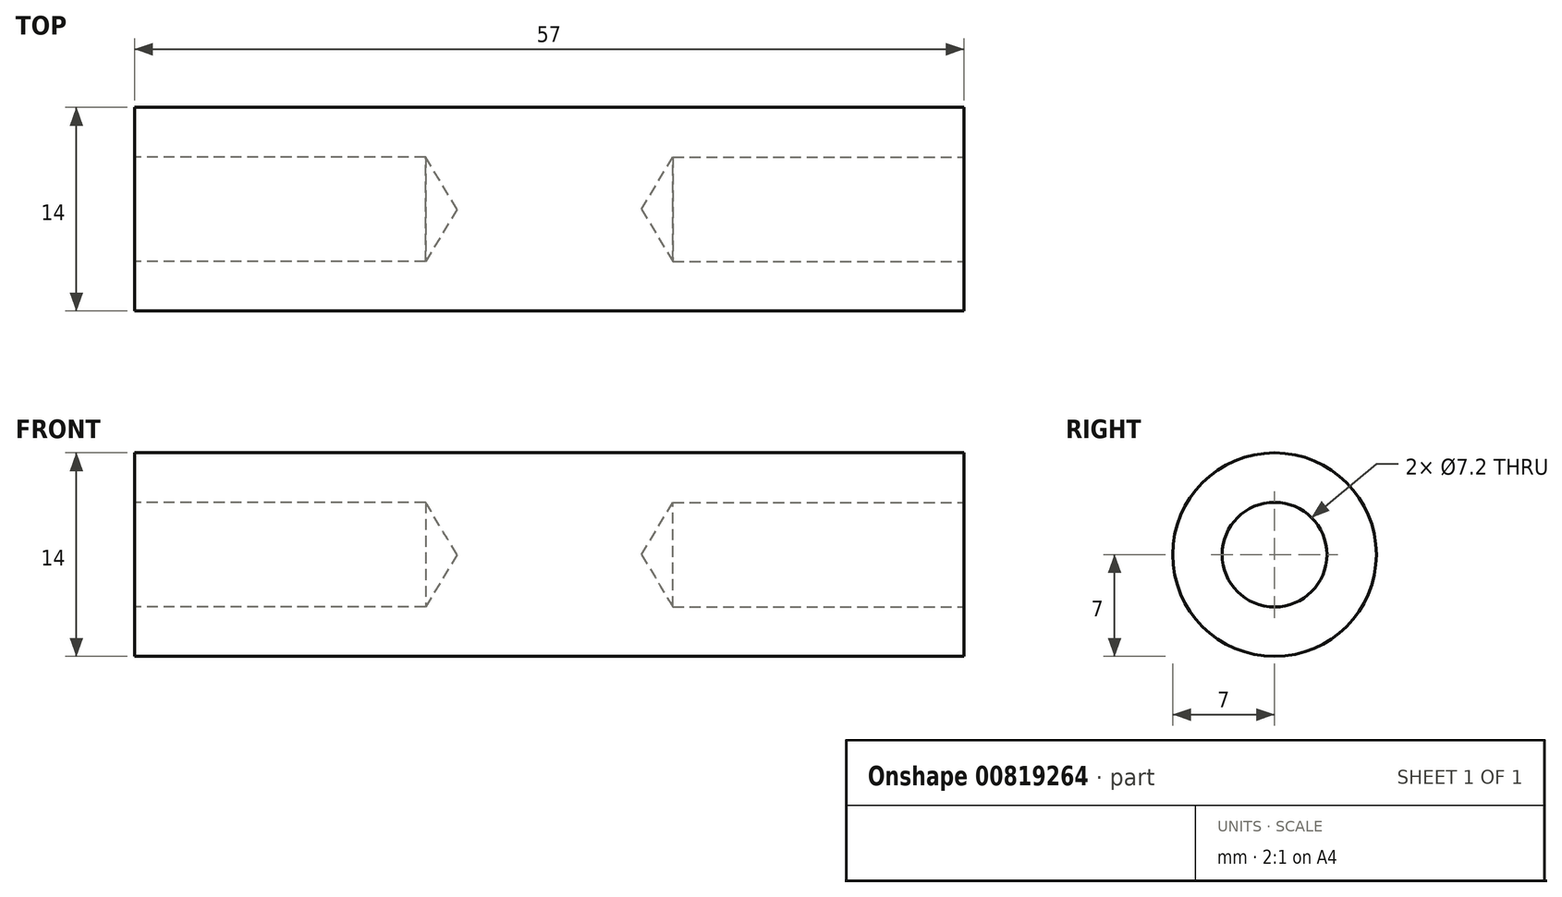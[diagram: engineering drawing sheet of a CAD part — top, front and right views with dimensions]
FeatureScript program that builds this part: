
annotation { "Feature Type Name" : "Feature", "Feature Type Description" : "" }
export const myFeature = defineFeature(function(context is Context, id is Id, definition is map)
    precondition{}
    {
        {
            var Q0;
            Q0=qCreatedBy(makeId("Front.planeOp"),FACE);
            var sketch = newSketch(context, id + "F0", { "sketchPlane" : qUnion([Q0])});
            skLineSegment(sketch, "E0.bottom", {"start": v(-28.5, 7) * mm, "end": v(28.5, 7) * mm});
            skLineSegment(sketch, "E0.top", {"start": v(-28.5, 0) * mm, "end": v(28.5, 0) * mm});
            skLineSegment(sketch, "E0.left", {"start": v(-28.5, 7) * mm, "end": v(-28.5, 0) * mm});
            skLineSegment(sketch, "E0.right", {"start": v(28.5, 7) * mm, "end": v(28.5, 0) * mm});
            skLineSegment(sketch, "E1", {"start": v(-53.81, 0) * mm, "end": v(44.44, 0) * mm, "construction": true});
            skSolve(sketch);
        }
        {
            var Q0;
            Q0=makeQuery(id+"F0.imprint","IMPRINT",FACE,{"disambiguationData":[TD([[makeQuery(id+"F0.imprint","IMPRINT",EDGE,{"derivedFrom":sQuery(id+"F0.wireOp",EDGE,"E0.bottom")}),-1.0]])]});
            var Q1;
            Q1=sQuery(id+"F0.wireOp",EDGE,"E1");
            var Q2;
            Q2=sQuery(id+"F0.wireOp",EDGE,"E1");
            revolve(context, id + "F1", {"surfaceOperationType" : NewSurfaceOperationType.NEW, "entities" : qUnion([Q0]), "surfaceEntities" : qUnion([Q1]), "axis" : qUnion([Q2]), "revolveType" : RevolveType.FULL});
        }
        {
            var Q0;
            Q0=makeQuery(id+"F1.opRevolve","SWEPT_FACE",FACE,{"disambiguationData":[OSD([sQuery(id+"F0.wireOp",EDGE,"E0.right")])]});
            var sketch = newSketch(context, id + "F2", { "sketchPlane" : qUnion([Q0])});
            skPoint(sketch, "E2", {"position": v(0, 0) * mm});
            skSolve(sketch);
        }
        {
            var Q0;
            Q0=sQuery(id+"F2.wireOp",VERTEX,"E2");
            var Q1;
            Q1=makeQuery(id+"F1.opRevolve","SWEPT_BODY",BODY,{"disambiguationData":[OSD([sQuery(id+"F0.wireOp",EDGE,"E0.bottom"),sQuery(id+"F0.wireOp",EDGE,"E0.top"),sQuery(id+"F0.wireOp",EDGE,"E0.left"),sQuery(id+"F0.wireOp",EDGE,"E0.right")])]});
            hole(context, id + "F3", {"style" : HoleStyle.SIMPLE, "endStyle" : HoleEndStyle.BLIND, "standardTappedOrClearance" : lookupTablePath({ "standard" : "ISO", "engagement" : "50%", "pitch" : "1.25 mm", "size" : "M8", "type" : "Tapped" }), "standardBlindInLast" : lookupTablePath({ "standard" : "ISO", "engagement" : "50%", "pitch" : "1.25 mm", "size" : "M8", "type" : "Tapped" }), "holeDiameter" : 7.2 * mm, "majorDiameter" : 8 * mm, "showTappedDepth" : true, "holeDepth" : 20 * mm, "isTappedThrough" : true, "tappedDepth" : 16.25 * mm, "tapClearance" : 3, "locations" : qUnion([Q0]), "scope" : qUnion([Q1])});
        }
        {
            var Q0;
            Q0=makeQuery(id+"F1.opRevolve","SWEPT_FACE",FACE,{"disambiguationData":[OSD([sQuery(id+"F0.wireOp",EDGE,"E0.left")])]});
            var sketch = newSketch(context, id + "F4", { "sketchPlane" : qUnion([Q0])});
            skPoint(sketch, "E3", {"position": v(0, 0) * mm});
            skSolve(sketch);
        }
        {
            var Q0;
            Q0=sQuery(id+"F4.wireOp",VERTEX,"E3");
            var Q1;
            Q1=makeQuery(id+"F1.opRevolve","SWEPT_BODY",BODY,{"disambiguationData":[OSD([sQuery(id+"F0.wireOp",EDGE,"E0.bottom"),sQuery(id+"F0.wireOp",EDGE,"E0.top"),sQuery(id+"F0.wireOp",EDGE,"E0.left"),sQuery(id+"F0.wireOp",EDGE,"E0.right")])]});
            hole(context, id + "F5", {"style" : HoleStyle.SIMPLE, "endStyle" : HoleEndStyle.BLIND, "standardTappedOrClearance" : lookupTablePath({ "standard" : "ISO", "engagement" : "50%", "pitch" : "1.25 mm", "size" : "M8", "type" : "Tapped" }), "standardBlindInLast" : lookupTablePath({ "standard" : "ISO", "engagement" : "50%", "pitch" : "1.25 mm", "size" : "M8", "type" : "Tapped" }), "holeDiameter" : 7.2 * mm, "majorDiameter" : 8 * mm, "showTappedDepth" : true, "holeDepth" : 20 * mm, "isTappedThrough" : true, "tappedDepth" : 16.25 * mm, "tapClearance" : 3, "locations" : qUnion([Q0]), "scope" : qUnion([Q1])});
        }
    });
